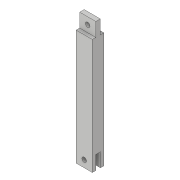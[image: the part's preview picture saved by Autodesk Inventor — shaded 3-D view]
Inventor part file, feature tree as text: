
AUTODESK INVENTOR PART (.ipt)
format: ipt  version: 2019 (Build 230136000, 136)  size: 122,880 bytes
history: native  units: mm
features: extrude x5, sketch x5
ambient origin geometry x8: Origin, YZ Plane, XZ Plane, XY Plane, X Axis, Y Axis, Z Axis, Center Point
bodies: Solid1 (feature_tree)
feature tree (10):
  extrude  "Extrusion1"  Depth=7.0mm
  extrude  "Extrusion2"  Depth=1.52mm
  extrude  "Extrusion3"  Depth=6.0mm TaperAngle=0.0deg
  extrude  "Extrusion4"  Depth=2.0mm
  extrude  "Extrusion6"  Depth=6.0mm TaperAngle=0.0deg
  sketch  "Sketch1"  dims[d0=5.0mm d1=7.0mm]
  sketch  "Sketch2"  dims[d2=50.0mm d3=0.0mm d4=1.52mm]
  sketch  "Sketch3"  dims[d5=1.52mm d6=6.0mm d7=0.0mm]
  sketch  "Sketch4"  dims[d8=2.0mm d9=3.5mm]
  sketch  "Sketch5"  dims[d10=3.0mm d11=6.0mm d12=0.0mm d13=1.48mm d14=1.48mm d15=6.0mm d16=0.0mm d17=3.0mm d18=3.5mm d19=2.0mm d26=10.0mm d27=0.0mm]
